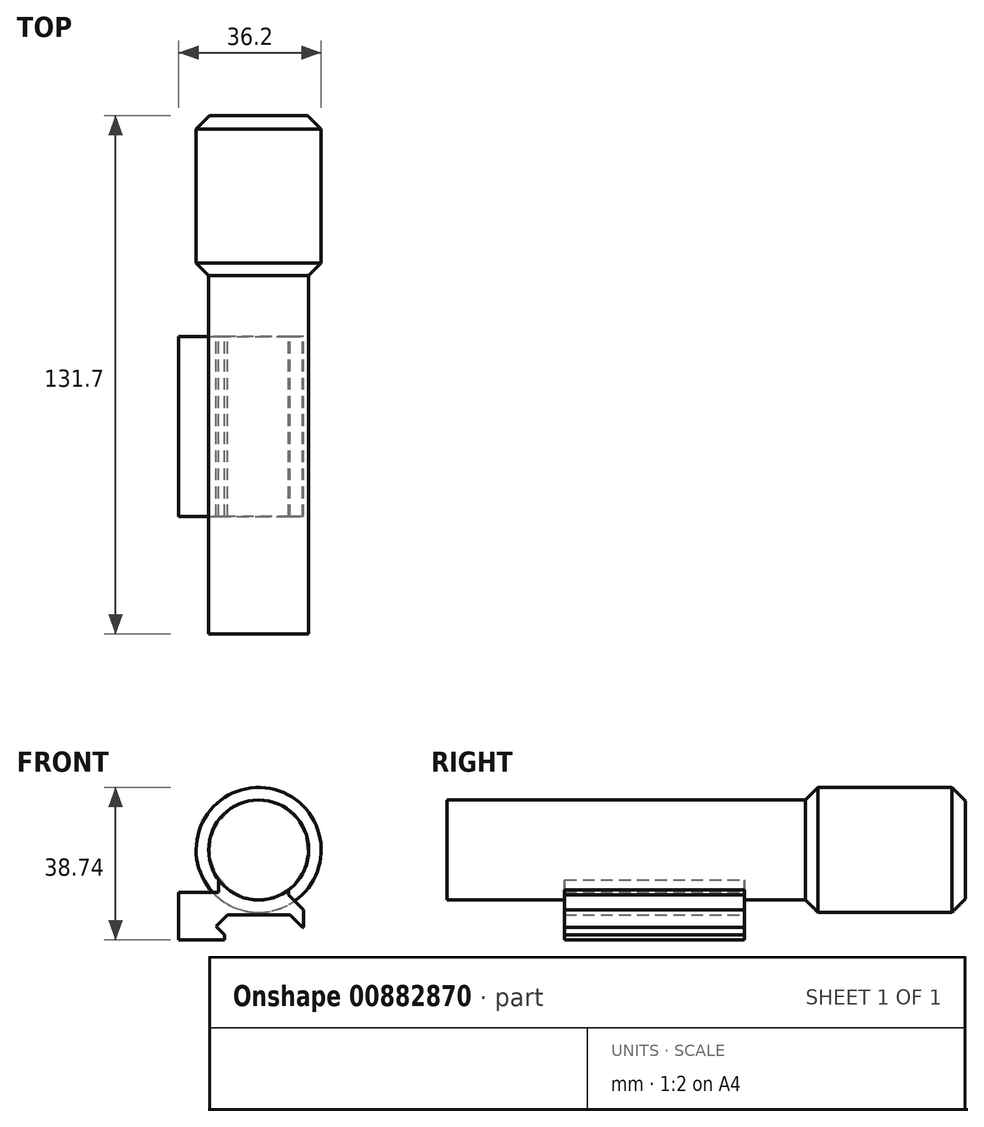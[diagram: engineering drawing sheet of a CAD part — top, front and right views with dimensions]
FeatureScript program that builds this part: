
annotation { "Feature Type Name" : "Feature", "Feature Type Description" : "" }
export const myFeature = defineFeature(function(context is Context, id is Id, definition is map)
    precondition{}
    {
        {
            var Q0;
            Q0=qCreatedBy(makeId("Top.planeOp"),FACE);
            var sketch = newSketch(context, id + "F0", { "sketchPlane" : qUnion([Q0])});
            skLineSegment(sketch, "E0", {"start": v(0, 15.48) * mm, "end": v(0, -17.28) * mm, "construction": true});
            skLineSegment(sketch, "E1", {"start": v(0, 78.98) * mm, "end": v(12.42, 78.98) * mm});
            skLineSegment(sketch, "E2", {"start": v(12.42, 78.98) * mm, "end": v(15.87, 75.52) * mm});
            skLineSegment(sketch, "E3", {"start": v(15.87, 75.52) * mm, "end": v(15.87, 41.51) * mm});
            skLineSegment(sketch, "E4", {"start": v(12.7, 38.34) * mm, "end": v(15.87, 41.51) * mm});
            skLineSegment(sketch, "E5", {"start": v(12.7, 38.34) * mm, "end": v(12.7, -52.72) * mm});
            skLineSegment(sketch, "E6", {"start": v(12.7, -52.72) * mm, "end": v(0, -52.72) * mm});
            skLineSegment(sketch, "E7", {"start": v(0, -52.72) * mm, "end": v(0, 78.98) * mm});
            skSolve(sketch);
        }
        {
            var Q0;
            Q0 = qSketchRegion(id + "F0", true);
            var Q1;
            Q1=sQuery(id+"F0.wireOp",EDGE,"E7");
            revolve(context, id + "F1", {"surfaceOperationType" : NewSurfaceOperationType.NEW, "entities" : qUnion([Q0]), "axis" : qUnion([Q1]), "revolveType" : RevolveType.FULL});
        }
        {
            var Q0;
            Q0=qCreatedBy(makeId("Front.planeOp"),FACE);
            var sketch = newSketch(context, id + "F2", { "sketchPlane" : qUnion([Q0])});
            skLineSegment(sketch, "E8", {"start": v(0, 4.3) * mm, "end": v(0, -12.7) * mm, "construction": true});
            skLineSegment(sketch, "E9", {"start": v(7.62, -10.16) * mm, "end": v(7.62, -11.43) * mm});
            skLineSegment(sketch, "E10", {"start": v(7.62, -11.43) * mm, "end": v(11.43, -15.24) * mm});
            skLineSegment(sketch, "E11", {"start": v(11.43, -15.24) * mm, "end": v(11.43, -19.69) * mm});
            skLineSegment(sketch, "E12", {"start": v(11.43, -19.69) * mm, "end": v(11.11, -19.69) * mm});
            skLineSegment(sketch, "E13", {"start": v(11.11, -19.69) * mm, "end": v(7.94, -16.51) * mm});
            skLineSegment(sketch, "E14", {"start": v(7.94, -16.51) * mm, "end": v(-7.94, -16.51) * mm});
            skLineSegment(sketch, "E15", {"start": v(-7.94, -16.51) * mm, "end": v(-10.83, -19.4) * mm});
            skLineSegment(sketch, "E16", {"start": v(-10.83, -19.4) * mm, "end": v(-8.64, -21.6) * mm});
            skLineSegment(sketch, "E17", {"start": v(-8.64, -21.6) * mm, "end": v(-8.64, -22.86) * mm});
            skLineSegment(sketch, "E18", {"start": v(-8.64, -22.86) * mm, "end": v(-20.32, -22.86) * mm});
            skLineSegment(sketch, "E19", {"start": v(-20.32, -22.86) * mm, "end": v(-20.32, -10.8) * mm});
            skLineSegment(sketch, "E20", {"start": v(-20.32, -10.8) * mm, "end": v(-10.16, -10.8) * mm});
            skLineSegment(sketch, "E21", {"start": v(-10.16, -10.8) * mm, "end": v(-10.16, -7.62) * mm});
            skCircle(sketch, "E22.0", {"center": v(0, 0) * mm, "radius": 12.7 * mm});
            skLineSegment(sketch, "E23", {"start": v(11.43, 1.8) * mm, "end": v(11.43, -4.7) * mm, "construction": true});
            skSolve(sketch);
        }
        {
            var Q0;
            {var subQ0=sQuery(id+"F2.wireOp",EDGE,"E9");Q0=makeQuery(id+"F2.imprint","IMPRINT",FACE,{"disambiguationData":[TD([[makeQuery(id+"F2.imprint","IMPRINT",EDGE,{"derivedFrom":subQ0}),-1.0]])]});}
            extrude(context, id + "F3", {"entities" : qUnion([Q0]), "operationType" : NewBodyOperationType.ADD, "endBound" : BoundingType.SYMMETRIC, "depth" : 45.72 * mm, "offsetDistance" : 25.4 * mm});
        }
    });
